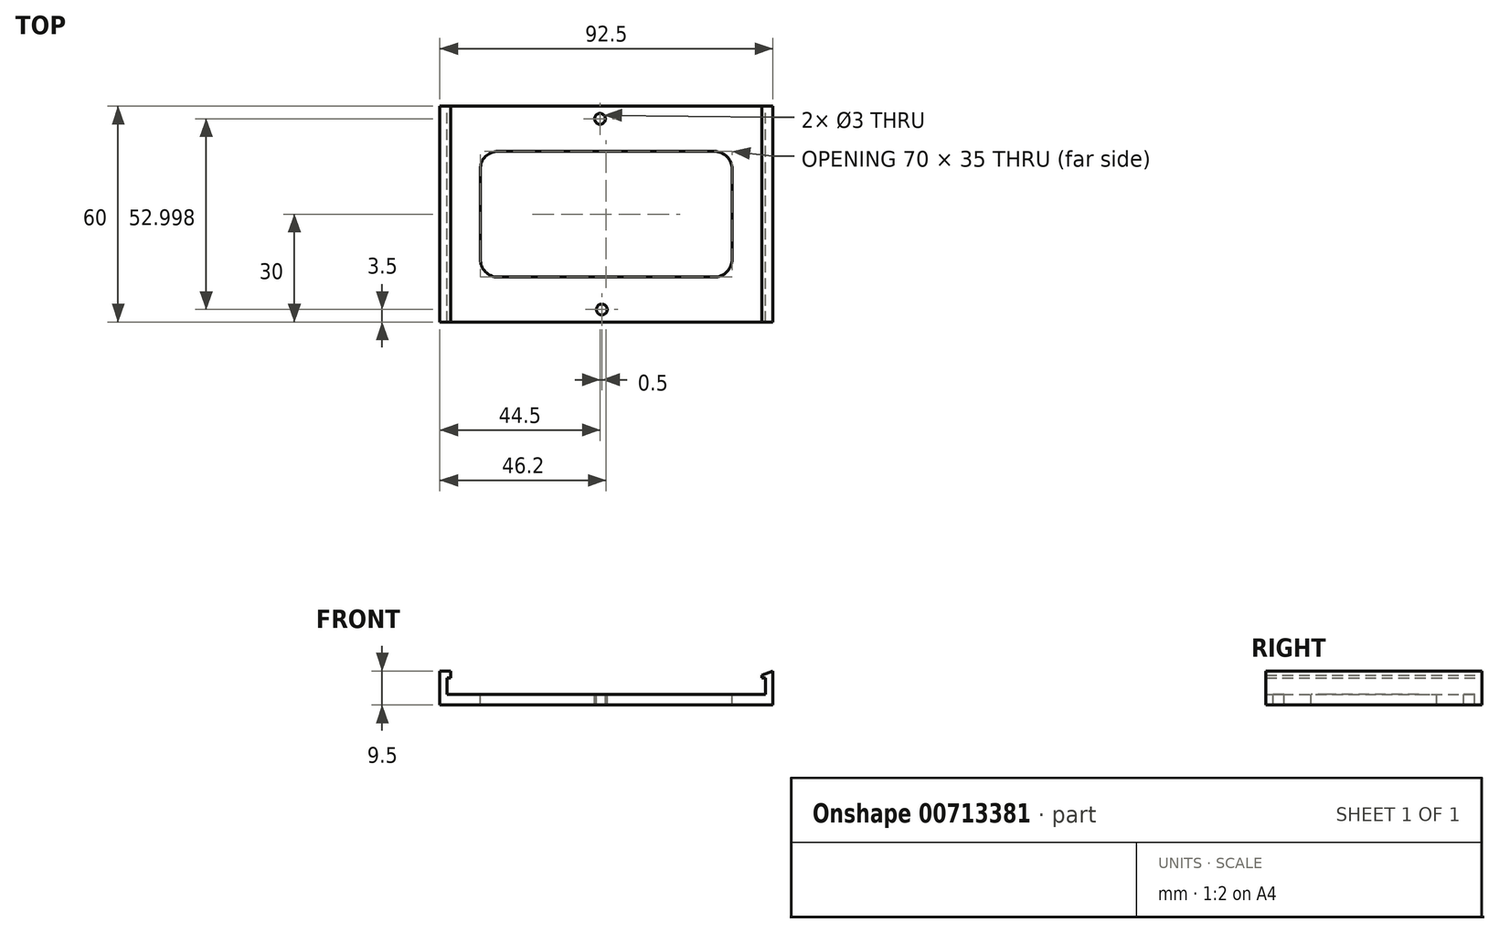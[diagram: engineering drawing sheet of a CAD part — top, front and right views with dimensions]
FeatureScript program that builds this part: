
annotation { "Feature Type Name" : "Feature", "Feature Type Description" : "" }
export const myFeature = defineFeature(function(context is Context, id is Id, definition is map)
    precondition{}
    {
        {
            var Q0;
            Q0=qCreatedBy(makeId("Front.planeOp"),FACE);
            var sketch = newSketch(context, id + "F0", { "sketchPlane" : qUnion([Q0])});
            skLineSegment(sketch, "E0", {"start": v(0, 0) * mm, "end": v(0, -3) * mm});
            skLineSegment(sketch, "E1", {"start": v(0, -3) * mm, "end": v(3, -3) * mm});
            skLineSegment(sketch, "E2", {"start": v(3, -3) * mm, "end": v(3, -3) * mm});
            skLineSegment(sketch, "E3", {"start": v(3, -3) * mm, "end": v(92.5, -3) * mm});
            skLineSegment(sketch, "E4", {"start": v(92.5, -3) * mm, "end": v(92.5, 0) * mm});
            skLineSegment(sketch, "E5", {"start": v(90.5, 0) * mm, "end": v(2, 0) * mm});
            skLineSegment(sketch, "E6", {"start": v(92.5, 0) * mm, "end": v(92.5, 6.4) * mm});
            skLineSegment(sketch, "E7", {"start": v(89.5, 4.5) * mm, "end": v(90.5, 4.5) * mm});
            skLineSegment(sketch, "E8", {"start": v(90.5, 4.5) * mm, "end": v(90.5, 0) * mm});
            skLineSegment(sketch, "E9", {"start": v(0, 0) * mm, "end": v(0, 6.5) * mm});
            skLineSegment(sketch, "E10", {"start": v(0, 6.5) * mm, "end": v(3, 6.5) * mm});
            skLineSegment(sketch, "E11", {"start": v(3, 6.5) * mm, "end": v(3, 4.5) * mm});
            skLineSegment(sketch, "E12", {"start": v(3, 4.5) * mm, "end": v(2, 4.5) * mm});
            skLineSegment(sketch, "E13", {"start": v(2, 4.5) * mm, "end": v(2, 0) * mm});
            skLineSegment(sketch, "E14", {"start": v(89.5, 4.5) * mm, "end": v(89.5, 5.27) * mm});
            skLineSegment(sketch, "E15", {"start": v(89.5, 5.27) * mm, "end": v(92.5, 6.4) * mm});
            skSolve(sketch);
        }
        {
            var Q0;
            Q0=qSketchRegion(id+"F0",true);
            extrude(context, id + "F1", {"entities" : qUnion([Q0]), "depth" : 60 * mm, "offsetDistance" : 25 * mm});
        }
        {
            var Q0;
            Q0=makeQuery(id+"F1.opExtrude","SWEPT_FACE",FACE,{"disambiguationData":[OSD([sQuery(id+"F0.wireOp",EDGE,"E5")])]});
            var sketch = newSketch(context, id + "F2", { "sketchPlane" : qUnion([Q0])});
            skCircle(sketch, "E16", {"center": v(45, -56.5) * mm, "radius": 1.5 * mm});
            skCircle(sketch, "E17", {"center": v(44.5, -3.5) * mm, "radius": 1.5 * mm});
            skSolve(sketch);
        }
        {
            var Q0;
            Q0 = qSketchRegion(id + "F2", true);
            extrude(context, id + "F3", {"entities" : qUnion([Q0]), "operationType" : NewBodyOperationType.REMOVE, "oppositeDirection" : true, "depth" : 25 * mm, "offsetDistance" : 25 * mm});
        }
        {
            var Q0;
            Q0=makeQuery(id+"F1.opExtrude","SWEPT_FACE",FACE,{"disambiguationData":[OSD([sQuery(id+"F0.wireOp",EDGE,"E5")])]});
            var sketch = newSketch(context, id + "F4", { "sketchPlane" : qUnion([Q0])});
            skLineSegment(sketch, "E18.bottom", {"start": v(11.2, -12.5) * mm, "end": v(81.2, -12.5) * mm});
            skLineSegment(sketch, "E18.top", {"start": v(11.2, -47.5) * mm, "end": v(81.2, -47.5) * mm});
            skLineSegment(sketch, "E18.left", {"start": v(11.2, -12.5) * mm, "end": v(11.2, -47.5) * mm});
            skLineSegment(sketch, "E18.right", {"start": v(81.2, -12.5) * mm, "end": v(81.2, -47.5) * mm});
            skSolve(sketch);
        }
        {
            var Q0;
            Q0=makeQuery(id+"F4.imprint","IMPRINT",FACE,{"disambiguationData":[TD([[makeQuery(id+"F4.imprint","IMPRINT",EDGE,{"derivedFrom":sQuery(id+"F4.wireOp",EDGE,"E18.bottom")}),-1.0]])]});
            extrude(context, id + "F5", {"entities" : qUnion([Q0]), "operationType" : NewBodyOperationType.REMOVE, "oppositeDirection" : true, "depth" : 25 * mm, "offsetDistance" : 25 * mm});
        }
        {
            var Q0;
            Q0=makeQuery(id+"F5.boolean.opBoolean","COPY",EDGE,{"derivedFrom":makeQuery(id+"F5.opExtrude","SWEPT_EDGE",EDGE,{"disambiguationData":[OSD([sQuery(id+"F4.wireOp",EDGE,"E18.bottom"),sQuery(id+"F4.wireOp",EDGE,"E18.left")])]})});
            var Q1;
            Q1=makeQuery(id+"F5.boolean.opBoolean","COPY",EDGE,{"derivedFrom":makeQuery(id+"F5.opExtrude","SWEPT_EDGE",EDGE,{"disambiguationData":[OSD([sQuery(id+"F4.wireOp",EDGE,"E18.top"),sQuery(id+"F4.wireOp",EDGE,"E18.right")])]})});
            var Q2;
            Q2=makeQuery(id+"F5.boolean.opBoolean","COPY",EDGE,{"derivedFrom":makeQuery(id+"F5.opExtrude","SWEPT_EDGE",EDGE,{"disambiguationData":[OSD([sQuery(id+"F4.wireOp",EDGE,"E18.bottom"),sQuery(id+"F4.wireOp",EDGE,"E18.right")])]})});
            var Q3;
            Q3=makeQuery(id+"F5.boolean.opBoolean","COPY",EDGE,{"derivedFrom":makeQuery(id+"F5.opExtrude","SWEPT_EDGE",EDGE,{"disambiguationData":[OSD([sQuery(id+"F4.wireOp",EDGE,"E18.top"),sQuery(id+"F4.wireOp",EDGE,"E18.left")])]})});
            fillet(context, id + "F6", {"entities" : qUnion([Q0, Q1, Q2, Q3]), "radius" : 5 * mm, "tangentPropagation" : true, "allowEdgeOverflow" : false});
        }
    });
